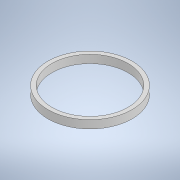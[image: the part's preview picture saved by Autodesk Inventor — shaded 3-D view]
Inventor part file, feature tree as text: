
AUTODESK INVENTOR PART (.ipt)
format: ipt  version: 2022.3 (Build 263350000, 350)  size: 101,888 bytes
history: native  units: mm
features: extrude x1, sketch x1
ambient origin geometry x8: Origin, YZ Plane, XZ Plane, XY Plane, X Axis, Y Axis, Z Axis, Center Point
bodies: Solid1 (feature_tree)
feature tree (2):
  extrude  "Extrusion1"  Depth=4.0mm
  sketch  "Sketch1"  dims[d0=41.8mm d1=2.0mm d2=4.0mm d3=0.0mm]
